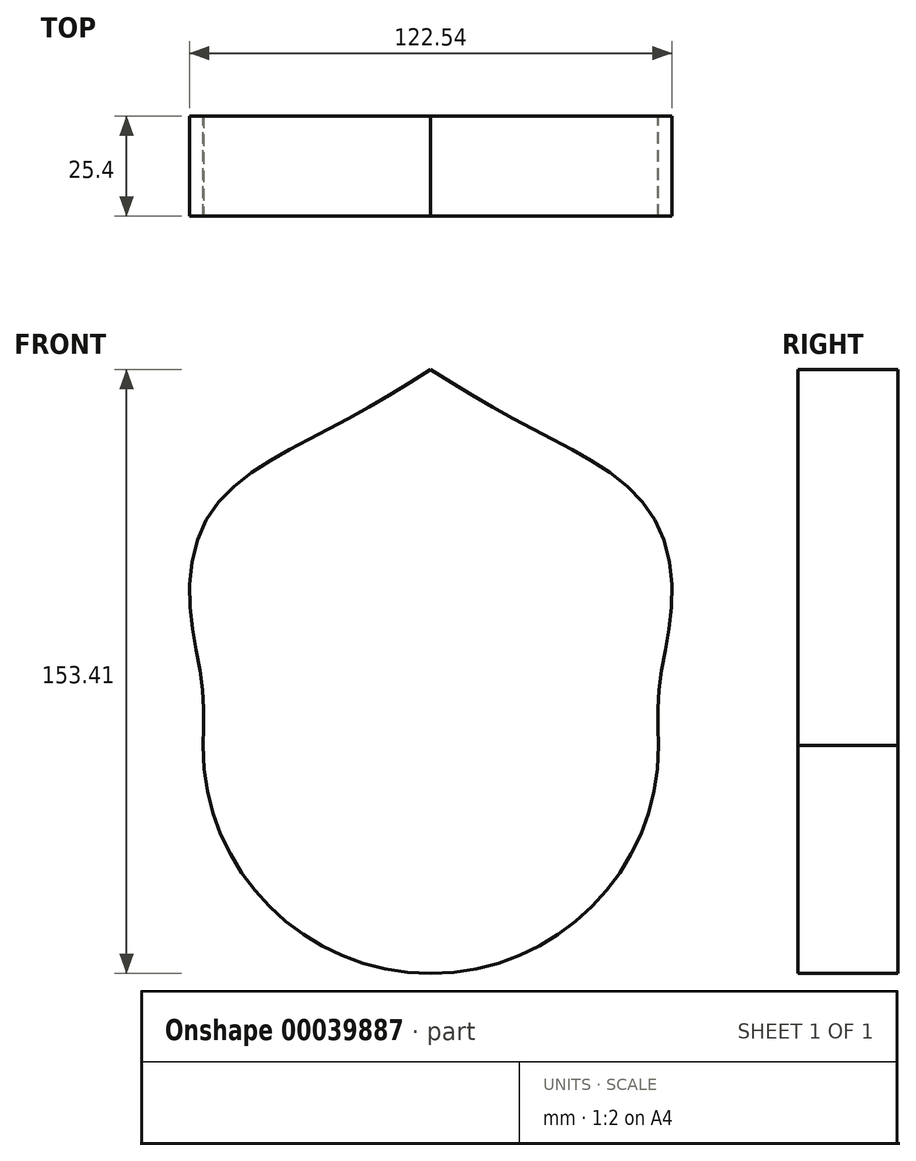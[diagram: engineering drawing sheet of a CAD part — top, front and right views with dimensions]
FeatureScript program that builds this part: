
annotation { "Feature Type Name" : "Feature", "Feature Type Description" : "" }
export const myFeature = defineFeature(function(context is Context, id is Id, definition is map)
    precondition{}
    {
        {
            var Q0;
            Q0=qCreatedBy(makeId("Front.planeOp"),FACE);
            var sketch = newSketch(context, id + "F0", { "sketchPlane" : qUnion([Q0])});
            skFitSpline(sketch, "E0", {"points": [v(57.9, 0) * mm, v(58.15, 15.58) * mm, v(61.15, 35.3) * mm, v(57.11, 57.11) * mm, v(41.53, 71.93) * mm, v(22.09, 82.44) * mm, v(0, 95.5) * mm], "startDerivative": vector(-4.26, 106.35) * mm, "endDerivative": vector(-121.26, 74.82) * mm});
            skFitSpline(sketch, "E1.MirrorCS", {"points": [v(-57.9, 0) * mm, v(-58.15, 15.58) * mm, v(-61.15, 35.3) * mm, v(-57.11, 57.11) * mm, v(-41.53, 71.93) * mm, v(-22.09, 82.44) * mm, v(0, 95.5) * mm], "startDerivative": vector(4.26, 106.35) * mm, "endDerivative": vector(121.26, 74.82) * mm});
            skArc(sketch, "E2", {"start": v(-57.9, 0) * mm, "mid": v(0, -57.9) * mm, "end": v(57.9, 0) * mm});
            skSolve(sketch);
        }
        {
            var Q0;
            Q0=makeQuery(id+"F0.imprint","IMPRINT",FACE,{"disambiguationData":[TD([[makeQuery(id+"F0.imprint","IMPRINT",EDGE,{"derivedFrom":sQuery(id+"F0.wireOp",EDGE,"E0")}),1.0]])]});
            extrude(context, id + "F1", {"entities" : qUnion([Q0]), "endBound" : BoundingType.SYMMETRIC, "depth" : 25.4 * mm});
        }
    });
